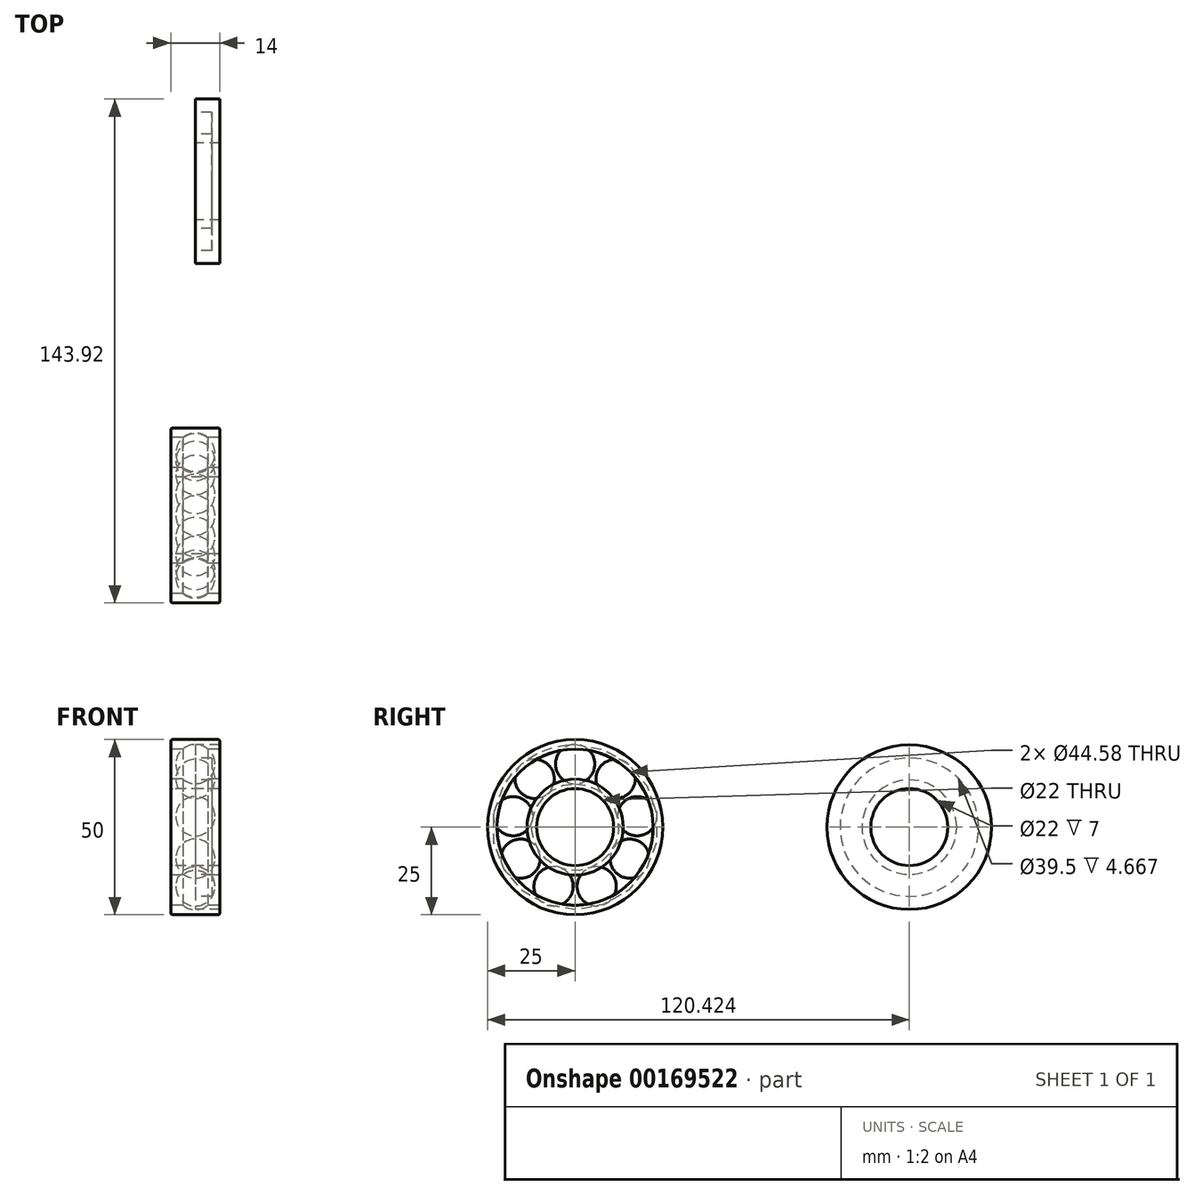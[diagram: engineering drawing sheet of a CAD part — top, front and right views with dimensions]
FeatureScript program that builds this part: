
annotation { "Feature Type Name" : "Feature", "Feature Type Description" : "" }
export const myFeature = defineFeature(function(context is Context, id is Id, definition is map)
    precondition{}
    {
        {
            assignVariable(context, id + "F0", {"name" : "InnerDia", "anyValue" : 22});
        }
        {
            assignVariable(context, id + "F1", {"name" : "Width", "anyValue" : 14});
        }
        {
            assignVariable(context, id + "F2", {"name" : "BallDia", "anyValue" : getVariable(context, 'Width') * 0.8});
        }
        {
            assignVariable(context, id + "F3", {"name" : "OuterDia", "anyValue" : getVariable(context, 'InnerDia') + getVariable(context, 'Width') * 2});
        }
        {
            assignVariable(context, id + "F4", {"name" : "NumBalls", "anyValue" : floor(((getVariable(context, 'InnerDia') + getVariable(context, 'OuterDia')) / 2 * PI / getVariable(context, 'BallDia')) - 1)});
        }
        {
            var Q0;
            Q0=qCreatedBy(makeId("Front.planeOp"),FACE);
            var sketch = newSketch(context, id + "F5", { "sketchPlane" : qUnion([Q0])});
            skLineSegment(sketch, "E0", {"start": v(-24.07, 0) * mm, "end": v(24.6, 0) * mm, "construction": true});
            skLineSegment(sketch, "E1", {"start": v(-6.5, 11) * mm, "end": v(6.5, 11) * mm});
            skLineSegment(sketch, "E2", {"start": v(7, 11.5) * mm, "end": v(7, 13.21) * mm});
            skLineSegment(sketch, "E3", {"start": v(6.5, 13.71) * mm, "end": v(3.6, 13.71) * mm});
            skLineSegment(sketch, "E4", {"start": v(-7, 11.5) * mm, "end": v(-7, 13.21) * mm});
            skLineSegment(sketch, "E5", {"start": v(-6.5, 13.71) * mm, "end": v(-3.6, 13.71) * mm});
            skLineSegment(sketch, "E6", {"start": v(0, 25.05) * mm, "end": v(0, -12.8) * mm, "construction": true});
            skLineSegment(sketch, "E7", {"start": v(-3.6, 22.29) * mm, "end": v(-6.5, 22.29) * mm});
            skLineSegment(sketch, "E8", {"start": v(-7, 22.79) * mm, "end": v(-7, 24.5) * mm});
            skLineSegment(sketch, "E9", {"start": v(-6.5, 25) * mm, "end": v(6.5, 25) * mm});
            skLineSegment(sketch, "E10", {"start": v(7, 24.5) * mm, "end": v(7, 22.79) * mm});
            skLineSegment(sketch, "E11", {"start": v(6.5, 22.29) * mm, "end": v(3.6, 22.29) * mm});
            skLineSegment(sketch, "E12", {"start": v(-9.29, 18) * mm, "end": v(9.44, 18) * mm, "construction": true});
            skArc(sketch, "E13", {"start": v(-3.6, 13.71) * mm, "mid": v(0, 12.4) * mm, "end": v(3.6, 13.71) * mm});
            skArc(sketch, "E14", {"start": v(-3.6, 22.29) * mm, "mid": v(0, 23.6) * mm, "end": v(3.6, 22.29) * mm});
            skPoint(sketch, "E15.visualSharp", {"position": v(-7, 25) * mm});
            skArc(sketch, "E15.filletArc", {"start": v(-6.5, 25) * mm, "mid": v(-6.85, 24.85) * mm, "end": v(-7, 24.5) * mm});
            skPoint(sketch, "E16.visualSharp", {"position": v(7, 25) * mm});
            skArc(sketch, "E16.filletArc", {"start": v(7, 24.5) * mm, "mid": v(6.85, 24.85) * mm, "end": v(6.5, 25) * mm});
            skPoint(sketch, "E17.visualSharp", {"position": v(7, 22.29) * mm});
            skArc(sketch, "E17.filletArc", {"start": v(6.5, 22.29) * mm, "mid": v(6.85, 22.44) * mm, "end": v(7, 22.79) * mm});
            skPoint(sketch, "E18.visualSharp", {"position": v(-7, 22.29) * mm});
            skArc(sketch, "E18.filletArc", {"start": v(-7, 22.79) * mm, "mid": v(-6.85, 22.44) * mm, "end": v(-6.5, 22.29) * mm});
            skPoint(sketch, "E19.visualSharp", {"position": v(-7, 13.71) * mm});
            skArc(sketch, "E19.filletArc", {"start": v(-6.5, 13.71) * mm, "mid": v(-6.85, 13.56) * mm, "end": v(-7, 13.21) * mm});
            skPoint(sketch, "E20.visualSharp", {"position": v(-7, 11) * mm});
            skArc(sketch, "E20.filletArc", {"start": v(-7, 11.5) * mm, "mid": v(-6.85, 11.15) * mm, "end": v(-6.5, 11) * mm});
            skPoint(sketch, "E21.visualSharp", {"position": v(7, 11) * mm});
            skArc(sketch, "E21.filletArc", {"start": v(6.5, 11) * mm, "mid": v(6.85, 11.15) * mm, "end": v(7, 11.5) * mm});
            skPoint(sketch, "E22.visualSharp", {"position": v(7, 13.71) * mm});
            skArc(sketch, "E22.filletArc", {"start": v(7, 13.21) * mm, "mid": v(6.85, 13.56) * mm, "end": v(6.5, 13.71) * mm});
            skSolve(sketch);
        }
        {
            var Q0;
            Q0 = qSketchRegion(id + "F5", true);
            var Q1;
            Q1=sQuery(id+"F5.wireOp",EDGE,"E0");
            revolve(context, id + "F6", {"entities" : qUnion([Q0]), "axis" : qUnion([Q1]), "revolveType" : RevolveType.FULL});
        }
        {
            var Q0;
            Q0=qCreatedBy(makeId("Front.planeOp"),FACE);
            var sketch = newSketch(context, id + "F7", { "sketchPlane" : qUnion([Q0])});
            skLineSegment(sketch, "E23", {"start": v(-7.6, 18) * mm, "end": v(8.4, 18) * mm, "construction": true});
            skLineSegment(sketch, "E24", {"start": v(0, 18.93) * mm, "end": v(0, 0) * mm, "construction": true});
            skArc(sketch, "E25", {"start": v(-5.6, 18) * mm, "mid": v(0, 23.6) * mm, "end": v(5.6, 18) * mm});
            skLineSegment(sketch, "E26", {"start": v(-5.6, 18) * mm, "end": v(5.6, 18) * mm});
            skSolve(sketch);
        }
        {
            var Q0;
            Q0 = qSketchRegion(id + "F7", true);
            var Q1;
            Q1=sQuery(id+"F7.wireOp",EDGE,"E23");
            revolve(context, id + "F8", {"entities" : qUnion([Q0]), "axis" : qUnion([Q1]), "revolveType" : RevolveType.FULL});
        }
        {
            var Q0;
            Q0=makeQuery(id+"F8.opRevolve","SWEPT_BODY",BODY,{"disambiguationData":[OSD([sQuery(id+"F7.wireOp",EDGE,"E25"),sQuery(id+"F7.wireOp",EDGE,"E26")])]});
            var Q1;
            Q1=makeQuery(id+"F6.opRevolve","SWEPT_EDGE",EDGE,{"disambiguationData":[OSD([sQuery(id+"F5.wireOp",EDGE,"E1"),sQuery(id+"F5.wireOp",EDGE,"E21.filletArc")])]});
            circularPattern(context, id + "F9", {"entities" : qUnion([Q0]), "axis" : qUnion([Q1]), "angle" : 360 * degree, "instanceCount" : getVariable(context, 'NumBalls'), "equalSpace" : true});
        }
        {
            var Q0;
            Q0=qCreatedBy(makeId("Top.planeOp"),FACE);
            var sketch = newSketch(context, id + "F10", { "sketchPlane" : qUnion([Q0])});
            skLineSegment(sketch, "E27", {"start": v(-38.8, 95.42) * mm, "end": v(40.8, 95.42) * mm, "construction": true});
            skLineSegment(sketch, "E28", {"start": v(0, 106.42) * mm, "end": v(7, 106.42) * mm});
            skLineSegment(sketch, "E29", {"start": v(7, 106.42) * mm, "end": v(7, 118.92) * mm});
            skLineSegment(sketch, "E30", {"start": v(7, 118.92) * mm, "end": v(0, 118.92) * mm});
            skLineSegment(sketch, "E31", {"start": v(0, 118.92) * mm, "end": v(0, 115.17) * mm});
            skLineSegment(sketch, "E32", {"start": v(0, 115.17) * mm, "end": v(4.67, 115.17) * mm});
            skLineSegment(sketch, "E33", {"start": v(4.67, 115.17) * mm, "end": v(4.67, 108.92) * mm});
            skLineSegment(sketch, "E34", {"start": v(4.67, 108.92) * mm, "end": v(0, 108.92) * mm});
            skLineSegment(sketch, "E35", {"start": v(0, 108.92) * mm, "end": v(0, 106.42) * mm});
            skSolve(sketch);
        }
        {
            var Q0;
            Q0 = qSketchRegion(id + "F10", true);
            var Q1;
            Q1=sQuery(id+"F10.wireOp",EDGE,"E27");
            revolve(context, id + "F11", {"entities" : qUnion([Q0]), "axis" : qUnion([Q1]), "revolveType" : RevolveType.FULL});
        }
    });
